# Revit family: Speciality_Equipment-Nixalite-Bird_Barrier_Strips_Model-H
name_source: partatom
category: Specialty Equipment
revit_build: Autodesk Revit Architecture 2012 (Build: 20110309_2315(x64)
units: mm (PartAtom-declared; Revit-internal decimal feet)

## types (2) — shared parameters
2 Foot Strip = 2' - 0"
4 Foot Strip = 4' - 0"
Assembly Code = E1090900
Default Elevation = 4' - 0"
Description = Premium Bird Barrier Strips
Manufacturer = Nixalite
Product Documentation Link = http://www.nixalite.com
Product Page URL = http://www.nixalite.com
Soft Tip Option = Yes
Spike Material = Metal - Nixalite - Stainless Steel - Black
Strip Material = Metal - Nixalite - Stainless Steel - Black
URL = http://www.nixalite.com

## per-type parameters (varying)
| type | Model |
| 4 Foot Strip | H |
| 2 Foot Strip | S |

type visibility flags: 2 boolean params named "<type name> Visibility" — each type sets only its own to Yes (folded from table)

## geometry (parser evidence)
native form markers: Sweep x5
no freeform markers — native parametric forms only
